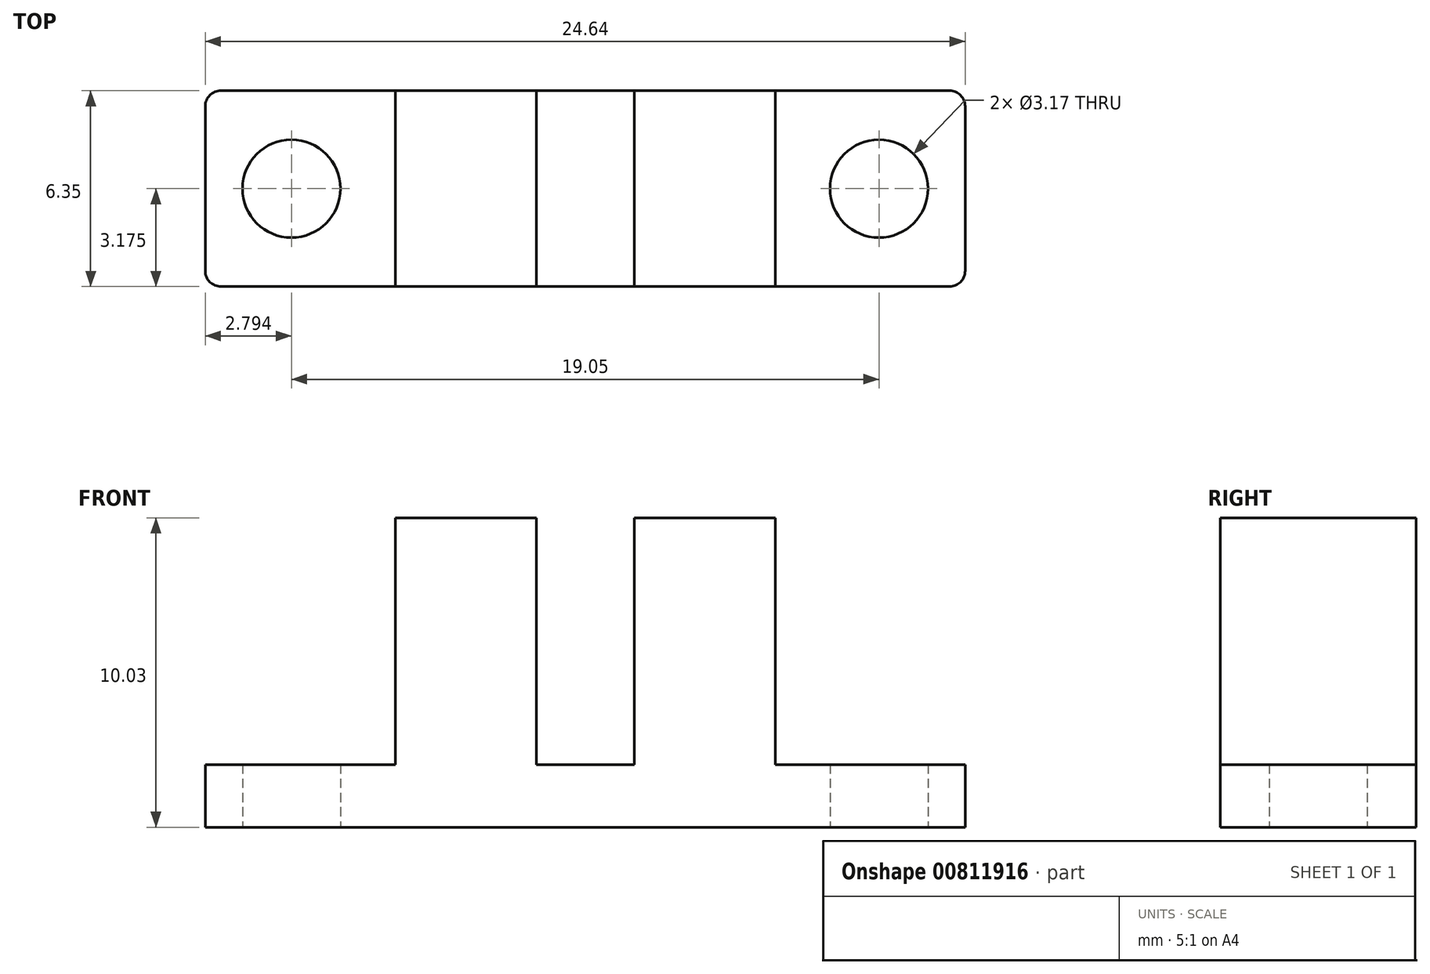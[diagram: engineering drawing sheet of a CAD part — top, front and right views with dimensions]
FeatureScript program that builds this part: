
annotation { "Feature Type Name" : "Feature", "Feature Type Description" : "" }
export const myFeature = defineFeature(function(context is Context, id is Id, definition is map)
    precondition{}
    {
        {
            var Q0;
            Q0=qCreatedBy(makeId("Top.planeOp"),FACE);
            var sketch = newSketch(context, id + "F0", { "sketchPlane" : qUnion([Q0])});
            skLineSegment(sketch, "E0.bottom", {"start": v(0.5, 0) * mm, "end": v(24.13, 0) * mm});
            skLineSegment(sketch, "E0.top", {"start": v(0.5, 6.35) * mm, "end": v(24.13, 6.35) * mm});
            skLineSegment(sketch, "E0.left", {"start": v(0, 0.5) * mm, "end": v(0, 5.84) * mm});
            skLineSegment(sketch, "E0.right", {"start": v(24.64, 0.5) * mm, "end": v(24.64, 5.84) * mm});
            skPoint(sketch, "E1.visualSharp", {"position": v(0, 6.35) * mm});
            skArc(sketch, "E1.filletArc", {"start": v(0.5, 6.35) * mm, "mid": v(0.15, 6.2) * mm, "end": v(0, 5.84) * mm});
            skPoint(sketch, "E2.visualSharp", {"position": v(0, 0) * mm});
            skArc(sketch, "E2.filletArc", {"start": v(0, 0.5) * mm, "mid": v(0.15, 0.15) * mm, "end": v(0.5, 0) * mm});
            skPoint(sketch, "E3.visualSharp", {"position": v(24.64, 0) * mm});
            skArc(sketch, "E3.filletArc", {"start": v(24.13, 0) * mm, "mid": v(24.49, 0.15) * mm, "end": v(24.64, 0.5) * mm});
            skPoint(sketch, "E4.visualSharp", {"position": v(24.64, 6.35) * mm});
            skArc(sketch, "E4.filletArc", {"start": v(24.64, 5.84) * mm, "mid": v(24.49, 6.2) * mm, "end": v(24.13, 6.35) * mm});
            skCircle(sketch, "E5", {"center": v(2.8, 3.18) * mm, "radius": 1.59 * mm});
            skCircle(sketch, "E6", {"center": v(21.84, 3.18) * mm, "radius": 1.59 * mm});
            skSolve(sketch);
        }
        {
            var Q0;
            Q0=qSketchRegion(id+"F0",true);
            extrude(context, id + "F1", {"entities" : qUnion([Q0]), "depth" : 2.03 * mm});
        }
        {
            var Q0;
            Q0=makeQuery(id+"F1.opExtrude","CAP_FACE",FACE,{"disambiguationData":[OSD([sQuery(id+"F0.wireOp",EDGE,"E0.bottom"),sQuery(id+"F0.wireOp",EDGE,"E0.top"),sQuery(id+"F0.wireOp",EDGE,"E0.left"),sQuery(id+"F0.wireOp",EDGE,"E0.right"),sQuery(id+"F0.wireOp",EDGE,"E1.filletArc"),sQuery(id+"F0.wireOp",EDGE,"E2.filletArc"),sQuery(id+"F0.wireOp",EDGE,"E3.filletArc"),sQuery(id+"F0.wireOp",EDGE,"E4.filletArc"),sQuery(id+"F0.wireOp",EDGE,"E5"),sQuery(id+"F0.wireOp",EDGE,"E6")])],"isStart":false});
            var sketch = newSketch(context, id + "F2", { "sketchPlane" : qUnion([Q0])});
            skLineSegment(sketch, "E7.bottom", {"start": v(6.16, 6.35) * mm, "end": v(10.73, 6.35) * mm});
            skLineSegment(sketch, "E7.top", {"start": v(6.16, 0) * mm, "end": v(10.73, 0) * mm});
            skLineSegment(sketch, "E7.left", {"start": v(6.16, 6.35) * mm, "end": v(6.16, 0) * mm});
            skLineSegment(sketch, "E7.right", {"start": v(10.73, 6.35) * mm, "end": v(10.73, 0) * mm});
            skLineSegment(sketch, "E8.bottom", {"start": v(13.9, 6.35) * mm, "end": v(18.48, 6.35) * mm});
            skLineSegment(sketch, "E8.top", {"start": v(13.9, 0) * mm, "end": v(18.48, 0) * mm});
            skLineSegment(sketch, "E8.left", {"start": v(13.9, 6.35) * mm, "end": v(13.9, 0) * mm});
            skLineSegment(sketch, "E8.right", {"start": v(18.48, 6.35) * mm, "end": v(18.48, 0) * mm});
            skSolve(sketch);
        }
        {
            var Q0;
            Q0=qSketchRegion(id+"F2",true);
            extrude(context, id + "F3", {"entities" : qUnion([Q0]), "operationType" : NewBodyOperationType.ADD, "depth" : 8 * mm});
        }
    });
